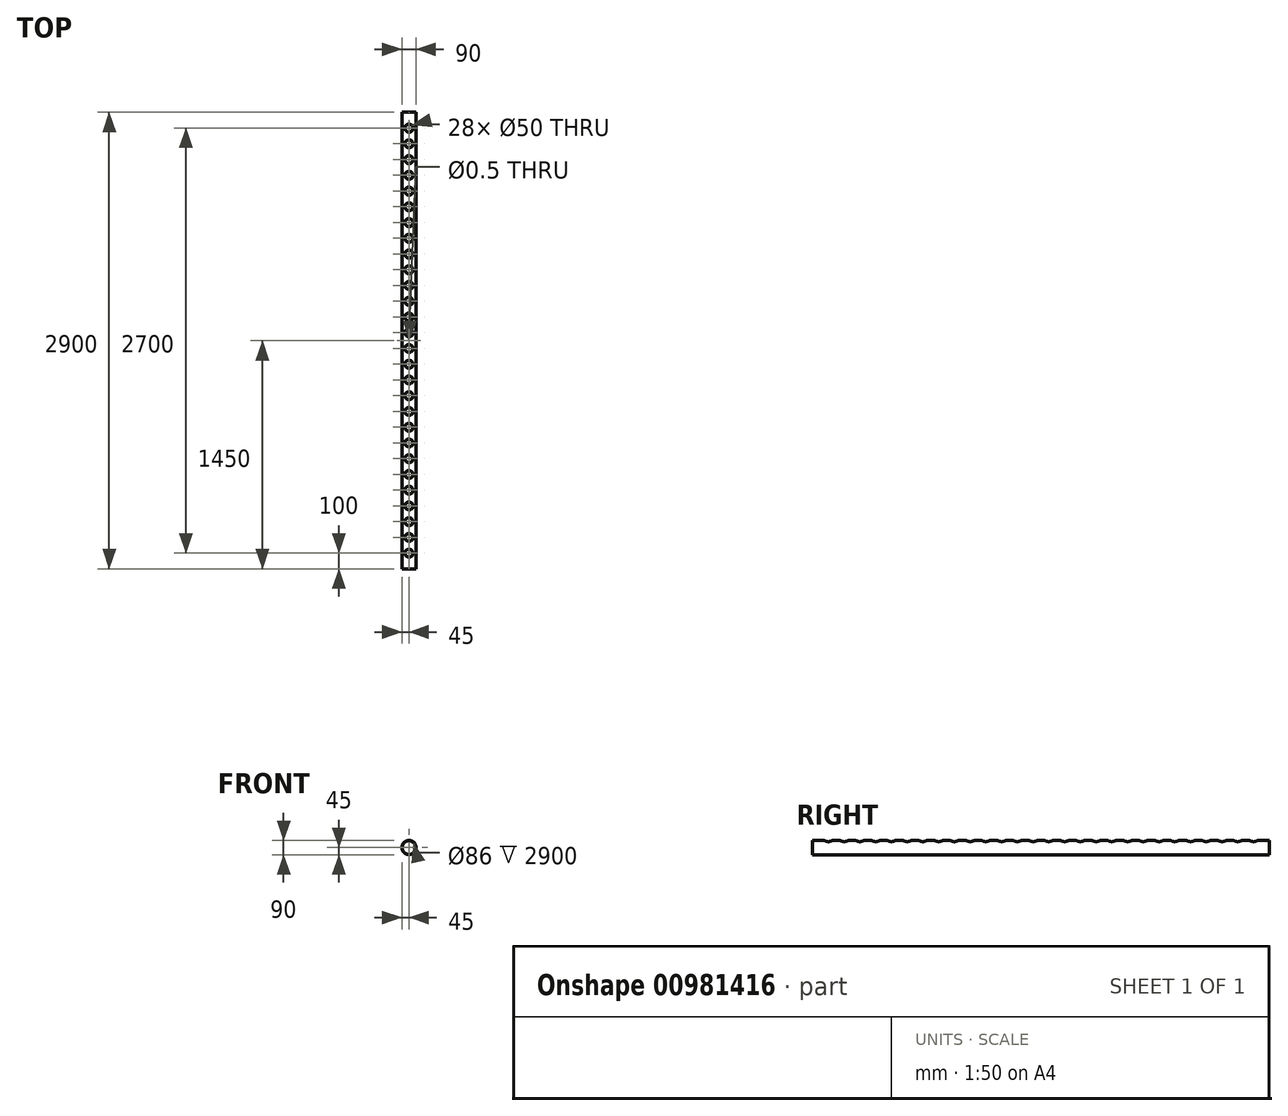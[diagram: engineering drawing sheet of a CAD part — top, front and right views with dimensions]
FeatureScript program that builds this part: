
annotation { "Feature Type Name" : "Feature", "Feature Type Description" : "" }
export const myFeature = defineFeature(function(context is Context, id is Id, definition is map)
    precondition{}
    {
        {
            var Q0;
            Q0=qCreatedBy(makeId("Front.planeOp"),FACE);
            var sketch = newSketch(context, id + "F0", { "sketchPlane" : qUnion([Q0])});
            skCircle(sketch, "E0", {"center": v(0, 0) * mm, "radius": 45 * mm});
            skCircle(sketch, "E1.0", {"center": v(0, 0) * mm, "radius": 43 * mm});
            skSolve(sketch);
        }
        {
            var Q0;
            Q0=qSketchRegion(id+"F0",true);
            extrude(context, id + "F1", {"entities" : qUnion([Q0]), "endBound" : BoundingType.SYMMETRIC, "depth" : 2900 * mm, "offsetDistance" : 25 * mm});
        }
        {
            var Q0;
            Q0=qCreatedBy(makeId("Top.planeOp"),FACE);
            cPlane(context, id + "F2", {"entities" : qUnion([Q0]), "cplaneType" : CPlaneType.OFFSET, "offset" : 45 * mm, "width" : 150 * mm, "height" : 150 * mm});
        }
        {
            var Q0;
            Q0=qCreatedBy(id+"F2.planeOp",FACE);
            var sketch = newSketch(context, id + "F3", { "sketchPlane" : qUnion([Q0])});
            skPoint(sketch, "E2", {"position": v(0, -1350) * mm});
            skPoint(sketch, "E3", {"position": v(0, -1250) * mm});
            skPoint(sketch, "E4", {"position": v(0, -1150) * mm});
            skPoint(sketch, "E5", {"position": v(0, -1050) * mm});
            skPoint(sketch, "E6", {"position": v(0, -950) * mm});
            skPoint(sketch, "E7", {"position": v(0, -850) * mm});
            skPoint(sketch, "E8", {"position": v(0, -750) * mm});
            skPoint(sketch, "E9", {"position": v(0, -650) * mm});
            skPoint(sketch, "E10", {"position": v(0, -550) * mm});
            skPoint(sketch, "E11", {"position": v(0, -450) * mm});
            skPoint(sketch, "E12", {"position": v(0, -350) * mm});
            skPoint(sketch, "E13", {"position": v(0, -250) * mm});
            skPoint(sketch, "E14", {"position": v(0, -150) * mm});
            skPoint(sketch, "E15", {"position": v(0, -50) * mm});
            skPoint(sketch, "E16", {"position": v(0, 50) * mm});
            skPoint(sketch, "E17", {"position": v(0, 150) * mm});
            skPoint(sketch, "E18", {"position": v(0, 250) * mm});
            skPoint(sketch, "E19", {"position": v(0, 350) * mm});
            skPoint(sketch, "E20", {"position": v(0, 450) * mm});
            skPoint(sketch, "E21", {"position": v(0, 550) * mm});
            skPoint(sketch, "E22", {"position": v(0, 650) * mm});
            skPoint(sketch, "E23", {"position": v(0, 750) * mm});
            skPoint(sketch, "E24", {"position": v(0, 850) * mm});
            skPoint(sketch, "E25", {"position": v(0, 950) * mm});
            skPoint(sketch, "E26", {"position": v(0, 1050) * mm});
            skPoint(sketch, "E27", {"position": v(0, 1150) * mm});
            skPoint(sketch, "E28", {"position": v(0, 1250) * mm});
            skPoint(sketch, "E29", {"position": v(0, 1350) * mm});
            skSolve(sketch);
        }
        {
            var Q0;
            Q0=sQuery(id+"F3.wireOp",VERTEX,"E2");
            var Q1;
            Q1=sQuery(id+"F3.wireOp",VERTEX,"E3");
            var Q2;
            Q2=sQuery(id+"F3.wireOp",VERTEX,"E4");
            var Q3;
            Q3=sQuery(id+"F3.wireOp",VERTEX,"E5");
            var Q4;
            Q4=sQuery(id+"F3.wireOp",VERTEX,"E6");
            var Q5;
            Q5=sQuery(id+"F3.wireOp",VERTEX,"E7");
            var Q6;
            Q6=sQuery(id+"F3.wireOp",VERTEX,"E8");
            var Q7;
            Q7=sQuery(id+"F3.wireOp",VERTEX,"E9");
            var Q8;
            Q8=sQuery(id+"F3.wireOp",VERTEX,"E10");
            var Q9;
            Q9=sQuery(id+"F3.wireOp",VERTEX,"E11");
            var Q10;
            Q10=sQuery(id+"F3.wireOp",VERTEX,"E12");
            var Q11;
            Q11=sQuery(id+"F3.wireOp",VERTEX,"E13");
            var Q12;
            Q12=sQuery(id+"F3.wireOp",VERTEX,"E14");
            var Q13;
            Q13=sQuery(id+"F3.wireOp",VERTEX,"E15");
            var Q14;
            Q14=sQuery(id+"F3.wireOp",VERTEX,"E16");
            var Q15;
            Q15=sQuery(id+"F3.wireOp",VERTEX,"E17");
            var Q16;
            Q16=sQuery(id+"F3.wireOp",VERTEX,"E18");
            var Q17;
            Q17=sQuery(id+"F3.wireOp",VERTEX,"E19");
            var Q18;
            Q18=sQuery(id+"F3.wireOp",VERTEX,"E20");
            var Q19;
            Q19=sQuery(id+"F3.wireOp",VERTEX,"E21");
            var Q20;
            Q20=sQuery(id+"F3.wireOp",VERTEX,"E22");
            var Q21;
            Q21=sQuery(id+"F3.wireOp",VERTEX,"E23");
            var Q22;
            Q22=sQuery(id+"F3.wireOp",VERTEX,"E24");
            var Q23;
            Q23=sQuery(id+"F3.wireOp",VERTEX,"E25");
            var Q24;
            Q24=sQuery(id+"F3.wireOp",VERTEX,"E26");
            var Q25;
            Q25=sQuery(id+"F3.wireOp",VERTEX,"E27");
            var Q26;
            Q26=sQuery(id+"F3.wireOp",VERTEX,"E28");
            var Q27;
            Q27=sQuery(id+"F3.wireOp",VERTEX,"E29");
            var Q28;
            Q28=sQuery(id+"F3.wireOp",VERTEX,"a31ac070-19d1-4092-b391-6f630edb761b");
            var Q29;
            Q29=makeQuery(id+"F1.opExtrude","SWEPT_BODY",BODY,{"disambiguationData":[OSD([sQuery(id+"F0.wireOp",EDGE,"E0"),sQuery(id+"F0.wireOp",EDGE,"E1.0")])]});
            hole(context, id + "F4", {"style" : HoleStyle.SIMPLE, "endStyle" : HoleEndStyle.BLIND, "holeDiameter" : 50 * mm, "majorDiameter" : 5 * mm, "holeDepth" : 50 * mm, "isTappedThrough" : true, "tappedDepth" : 12 * mm, "tapClearance" : 3, "startFromSketch" : true, "locations" : qUnion([Q0, Q1, Q2, Q3, Q4, Q5, Q6, Q7, Q8, Q9, Q10, Q11, Q12, Q13, Q14, Q15, Q16, Q17, Q18, Q19, Q20, Q21, Q22, Q23, Q24, Q25, Q26, Q27, Q28]), "scope" : qUnion([Q29])});
        }
        {
            var Q0;
            Q0=qCreatedBy(makeId("Top.planeOp"),FACE);
            var sketch = newSketch(context, id + "F5", { "sketchPlane" : qUnion([Q0])});
            skPoint(sketch, "E30", {"position": v(0, 0) * mm});
            skSolve(sketch);
        }
        {
            var Q0;
            Q0=sQuery(id+"F5.wireOp",VERTEX,"E30");
            var Q1;
            Q1=makeQuery(id+"F1.opExtrude","SWEPT_BODY",BODY,{"disambiguationData":[OSD([sQuery(id+"F0.wireOp",EDGE,"E0"),sQuery(id+"F0.wireOp",EDGE,"E1.0")])]});
            hole(context, id + "F6", {"style" : HoleStyle.SIMPLE, "endStyle" : HoleEndStyle.BLIND, "holeDiameter" : 0.5 * mm, "majorDiameter" : 5 * mm, "holeDepth" : 50 * mm, "isTappedThrough" : true, "tappedDepth" : 12 * mm, "tapClearance" : 3, "startFromSketch" : true, "locations" : qUnion([Q0]), "scope" : qUnion([Q1])});
        }
    });
